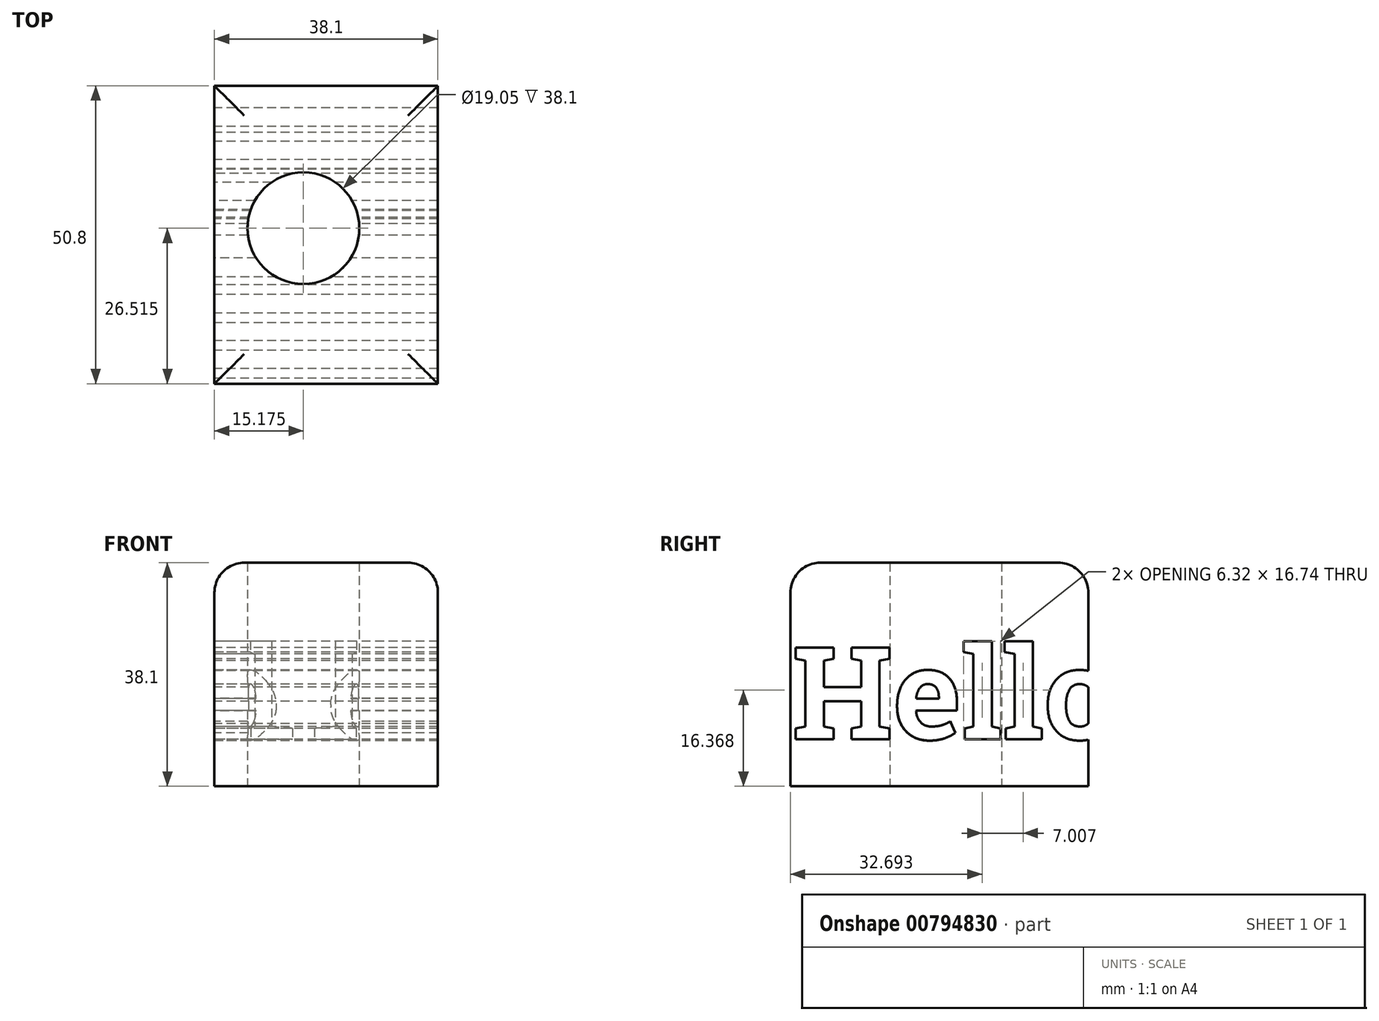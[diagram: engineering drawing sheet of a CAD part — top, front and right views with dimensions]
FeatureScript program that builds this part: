
annotation { "Feature Type Name" : "Feature", "Feature Type Description" : "" }
export const myFeature = defineFeature(function(context is Context, id is Id, definition is map)
    precondition{}
    {
        {
            var Q0;
            Q0=qCreatedBy(makeId("Front.planeOp"),FACE);
            var sketch = newSketch(context, id + "F0", { "sketchPlane" : qUnion([Q0])});
            skLineSegment(sketch, "E0", {"start": v(0, 38.1) * mm, "end": v(0, 0) * mm});
            skLineSegment(sketch, "E1", {"start": v(0, 0) * mm, "end": v(38.1, 0) * mm});
            skLineSegment(sketch, "E2", {"start": v(38.1, 0) * mm, "end": v(38.1, 38.1) * mm});
            skLineSegment(sketch, "E3", {"start": v(38.1, 38.1) * mm, "end": v(0, 38.1) * mm});
            skSolve(sketch);
        }
        {
            var Q0;
            Q0 = qSketchRegion(id + "F0", true);
            extrude(context, id + "F1", {"entities" : qUnion([Q0]), "depth" : 50.8 * mm, "offsetDistance" : 25.4 * mm});
        }
        {
            var Q0;
            Q0=qCreatedBy(makeId("Top.planeOp"),FACE);
            var sketch = newSketch(context, id + "F2", { "sketchPlane" : qUnion([Q0])});
            skCircle(sketch, "E4", {"center": v(15.17, -24.28) * mm, "radius": 9.53 * mm});
            skSolve(sketch);
        }
        {
            var Q0;
            Q0 = qSketchRegion(id + "F2", true);
            extrude(context, id + "F3", {"entities" : qUnion([Q0]), "operationType" : NewBodyOperationType.REMOVE, "endBound" : BoundingType.THROUGH_ALL, "depth" : 25.4 * mm, "offsetDistance" : 25.4 * mm});
        }
        {
            var Q0;
            Q0=makeQuery(id+"F1.opExtrude","SWEPT_EDGE",EDGE,{"disambiguationData":[OSD([sQuery(id+"F0.wireOp",EDGE,"E0"),sQuery(id+"F0.wireOp",EDGE,"E3")])]});
            var Q1;
            Q1=makeQuery(id+"F1.opExtrude","CAP_EDGE",EDGE,{"disambiguationData":[OSD([sQuery(id+"F0.wireOp",EDGE,"E3")])],"isStart":true});
            var Q2;
            Q2=makeQuery(id+"F1.opExtrude","SWEPT_EDGE",EDGE,{"disambiguationData":[OSD([sQuery(id+"F0.wireOp",EDGE,"E2"),sQuery(id+"F0.wireOp",EDGE,"E3")])]});
            var Q3;
            Q3=makeQuery(id+"F1.opExtrude","CAP_EDGE",EDGE,{"disambiguationData":[OSD([sQuery(id+"F0.wireOp",EDGE,"E3")])],"isStart":false});
            fillet(context, id + "F4", {"entities" : qUnion([Q0, Q1, Q2, Q3]), "radius" : 5.08 * mm, "tangentPropagation" : true, "allowEdgeOverflow" : false});
        }
        {
            var Q0;
            Q0=qCreatedBy(makeId("Right.planeOp"),FACE);
            var sketch = newSketch(context, id + "F5", { "sketchPlane" : qUnion([Q0])});
            skText(sketch, "E5", { "text": "Hello", "fontName": "RobotoSlab-Bold.ttf"});
            const initialGuessF5  = {"E5": [-0.05049, 0.008, 1, 0, 0.01582]};
            skSetInitialGuess(sketch, initialGuessF5);
            skSolve(sketch);
        }
        {
            var Q0;
            Q0 = qSketchRegion(id + "F5", true);
            extrude(context, id + "F6", {"entities" : qUnion([Q0]), "operationType" : NewBodyOperationType.REMOVE, "endBound" : BoundingType.THROUGH_ALL, "depth" : 25.4 * mm, "offsetDistance" : 25.4 * mm});
        }
    });
